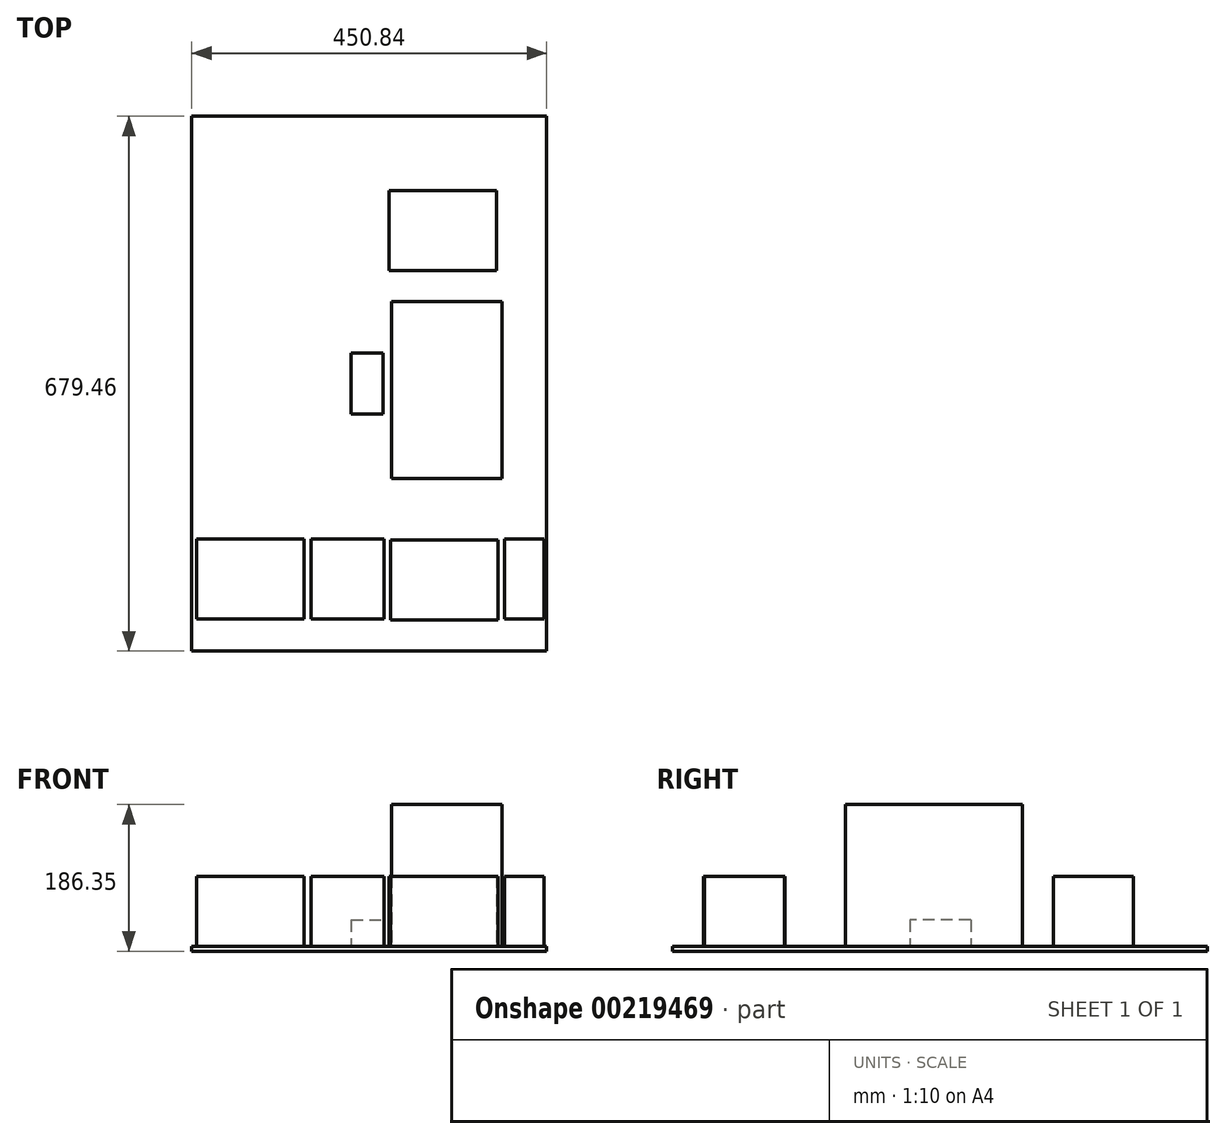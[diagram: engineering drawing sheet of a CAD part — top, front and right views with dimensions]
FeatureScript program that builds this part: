
annotation { "Feature Type Name" : "Feature", "Feature Type Description" : "" }
export const myFeature = defineFeature(function(context is Context, id is Id, definition is map)
    precondition{}
    {
        {
            var Q0;
            Q0=qCreatedBy(makeId("Top.planeOp"),FACE);
            var sketch = newSketch(context, id + "F0", { "sketchPlane" : qUnion([Q0])});
            skLineSegment(sketch, "E0.bottom", {"start": v(-225.42, -339.73) * mm, "end": v(225.43, -339.73) * mm});
            skLineSegment(sketch, "E0.top", {"start": v(-225.43, 339.72) * mm, "end": v(225.42, 339.72) * mm});
            skLineSegment(sketch, "E0.left", {"start": v(-225.42, -339.73) * mm, "end": v(-225.43, 339.73) * mm});
            skLineSegment(sketch, "E0.right", {"start": v(225.43, -339.73) * mm, "end": v(225.42, 339.72) * mm});
            skPoint(sketch, "E0.middle", {"position": v(0, 0) * mm});
            skSolve(sketch);
        }
        {
            var Q0;
            Q0=makeQuery(id+"F0.imprint","IMPRINT",FACE,{"disambiguationData":[TD([[makeQuery(id+"F0.imprint","IMPRINT",EDGE,{"derivedFrom":sQuery(id+"F0.wireOp",EDGE,"E0.bottom")}),1.0]])]});
            extrude(context, id + "F1", {"entities" : qUnion([Q0]), "oppositeDirection" : true, "depth" : 6.35 * mm});
        }
        {
            var Q0;
            Q0=makeQuery(id+"F1.opExtrude","CAP_FACE",FACE,{"disambiguationData":[OSD([sQuery(id+"F0.wireOp",EDGE,"E0.bottom"),sQuery(id+"F0.wireOp",EDGE,"E0.top"),sQuery(id+"F0.wireOp",EDGE,"E0.left"),sQuery(id+"F0.wireOp",EDGE,"E0.right")])],"isStart":true});
            var sketch = newSketch(context, id + "F2", { "sketchPlane" : qUnion([Q0])});
            skLineSegment(sketch, "E1.bottom", {"start": v(34.75, -122.57) * mm, "end": v(170.9, -122.57) * mm});
            skLineSegment(sketch, "E1.top", {"start": v(34.75, -224.17) * mm, "end": v(170.9, -224.17) * mm});
            skLineSegment(sketch, "E1.left", {"start": v(34.75, -122.57) * mm, "end": v(34.75, -224.17) * mm});
            skLineSegment(sketch, "E1.right", {"start": v(170.9, -122.57) * mm, "end": v(170.9, -224.17) * mm});
            skSolve(sketch);
        }
        {
            var Q0;
            Q0 = qSketchRegion(id + "F2", true);
            extrude(context, id + "F3", {"entities" : qUnion([Q0]), "depth" : 88.9 * mm, "offsetDistance" : 25.4 * mm});
        }
        {
            var Q0;
            Q0=makeQuery(id+"F1.opExtrude","CAP_FACE",FACE,{"disambiguationData":[OSD([sQuery(id+"F0.wireOp",EDGE,"E0.bottom"),sQuery(id+"F0.wireOp",EDGE,"E0.top"),sQuery(id+"F0.wireOp",EDGE,"E0.left"),sQuery(id+"F0.wireOp",EDGE,"E0.right")])],"isStart":true});
            var sketch = newSketch(context, id + "F4", { "sketchPlane" : qUnion([Q0])});
            skLineSegment(sketch, "E2.bottom", {"start": v(0, 209.73) * mm, "end": v(136.14, 209.73) * mm});
            skLineSegment(sketch, "E2.top", {"start": v(0, 108.13) * mm, "end": v(136.14, 108.13) * mm});
            skLineSegment(sketch, "E2.left", {"start": v(0, 209.73) * mm, "end": v(0, 108.13) * mm});
            skLineSegment(sketch, "E2.right", {"start": v(136.14, 209.73) * mm, "end": v(136.14, 108.13) * mm});
            skSolve(sketch);
        }
        {
            var Q0;
            Q0=makeQuery(id+"F4.imprint","IMPRINT",FACE,{"disambiguationData":[TD([[makeQuery(id+"F4.imprint","IMPRINT",EDGE,{"derivedFrom":sQuery(id+"F4.wireOp",EDGE,"E2.bottom")}),-1.0]])]});
            extrude(context, id + "F5", {"entities" : qUnion([Q0]), "depth" : 88.9 * mm, "offsetDistance" : 25.4 * mm});
        }
        {
            var Q0;
            Q0=makeQuery(id+"F1.opExtrude","CAP_FACE",FACE,{"disambiguationData":[OSD([sQuery(id+"F0.wireOp",EDGE,"E0.bottom"),sQuery(id+"F0.wireOp",EDGE,"E0.top"),sQuery(id+"F0.wireOp",EDGE,"E0.left"),sQuery(id+"F0.wireOp",EDGE,"E0.right")])],"isStart":true});
            var sketch = newSketch(context, id + "F6", { "sketchPlane" : qUnion([Q0])});
            skLineSegment(sketch, "E3.bottom", {"start": v(8.27, -126.38) * mm, "end": v(-41.51, -126.38) * mm});
            skLineSegment(sketch, "E3.top", {"start": v(8.27, -227.98) * mm, "end": v(-41.51, -227.98) * mm});
            skLineSegment(sketch, "E3.left", {"start": v(8.27, -126.38) * mm, "end": v(8.27, -227.98) * mm});
            skLineSegment(sketch, "E3.right", {"start": v(-41.51, -126.38) * mm, "end": v(-41.51, -227.98) * mm});
            skSolve(sketch);
        }
        {
            var Q0;
            Q0 = qSketchRegion(id + "F6", true);
            extrude(context, id + "F7", {"entities" : qUnion([Q0]), "depth" : 88.9 * mm, "offsetDistance" : 25.4 * mm});
        }
        {
            var Q0;
            Q0=makeQuery(id+"F1.opExtrude","CAP_FACE",FACE,{"disambiguationData":[OSD([sQuery(id+"F0.wireOp",EDGE,"E0.bottom"),sQuery(id+"F0.wireOp",EDGE,"E0.top"),sQuery(id+"F0.wireOp",EDGE,"E0.left"),sQuery(id+"F0.wireOp",EDGE,"E0.right")])],"isStart":true});
            var sketch = newSketch(context, id + "F8", { "sketchPlane" : qUnion([Q0])});
            skLineSegment(sketch, "E4.bottom", {"start": v(-221.8, -125.98) * mm, "end": v(-85.66, -125.98) * mm});
            skLineSegment(sketch, "E4.top", {"start": v(-221.8, -227.58) * mm, "end": v(-85.66, -227.58) * mm});
            skLineSegment(sketch, "E4.left", {"start": v(-221.8, -125.98) * mm, "end": v(-221.8, -227.58) * mm});
            skLineSegment(sketch, "E4.right", {"start": v(-85.66, -125.98) * mm, "end": v(-85.66, -227.58) * mm});
            skSolve(sketch);
        }
        {
            var Q0;
            Q0 = qSketchRegion(id + "F8", true);
            extrude(context, id + "F9", {"entities" : qUnion([Q0]), "depth" : 88.9 * mm, "offsetDistance" : 25.4 * mm});
        }
        {
            var Q0;
            Q0=makeQuery(id+"F3.opExtrude","SWEPT_BODY",BODY,{"disambiguationData":[OSD([sQuery(id+"F2.wireOp",EDGE,"E1.bottom"),sQuery(id+"F2.wireOp",EDGE,"E1.top"),sQuery(id+"F2.wireOp",EDGE,"E1.left"),sQuery(id+"F2.wireOp",EDGE,"E1.right")])]});
            transform(context, id + "F10", {"entities" : qUnion([Q0]), "transformType" : TransformType.TRANSLATION_3D, "dx" : -7.62 * mm, "dy" : -76.2 * mm, "dz" : 0 * mm, "makeCopy" : false});
        }
        {
            var Q0;
            Q0=makeQuery(id+"F7.opExtrude","SWEPT_BODY",BODY,{"disambiguationData":[OSD([sQuery(id+"F6.wireOp",EDGE,"E3.bottom"),sQuery(id+"F6.wireOp",EDGE,"E3.top"),sQuery(id+"F6.wireOp",EDGE,"E3.left"),sQuery(id+"F6.wireOp",EDGE,"E3.right")])]});
            transform(context, id + "F11", {"entities" : qUnion([Q0]), "transformType" : TransformType.TRANSLATION_3D, "dx" : 213.36 * mm, "dy" : -71.12 * mm, "dz" : 0 * mm, "makeCopy" : false});
        }
        {
            var Q0;
            Q0=makeQuery(id+"F9.opExtrude","SWEPT_BODY",BODY,{"disambiguationData":[OSD([sQuery(id+"F8.wireOp",EDGE,"E4.bottom"),sQuery(id+"F8.wireOp",EDGE,"E4.top"),sQuery(id+"F8.wireOp",EDGE,"E4.left"),sQuery(id+"F8.wireOp",EDGE,"E4.right")])]});
            transform(context, id + "F12", {"entities" : qUnion([Q0]), "transformType" : TransformType.TRANSLATION_3D, "dx" : 2.54 * mm, "dy" : -71.12 * mm, "dz" : 0 * mm, "makeCopy" : false});
        }
        {
            var Q0;
            Q0=makeQuery(id+"F1.opExtrude","CAP_FACE",FACE,{"disambiguationData":[OSD([sQuery(id+"F0.wireOp",EDGE,"E0.bottom"),sQuery(id+"F0.wireOp",EDGE,"E0.top"),sQuery(id+"F0.wireOp",EDGE,"E0.left"),sQuery(id+"F0.wireOp",EDGE,"E0.right")])],"isStart":true});
            var sketch = newSketch(context, id + "F13", { "sketchPlane" : qUnion([Q0])});
            skLineSegment(sketch, "E5.bottom", {"start": v(-109.58, -197.58) * mm, "end": v(-16.62, -197.58) * mm});
            skLineSegment(sketch, "E5.top", {"start": v(-109.58, -299.18) * mm, "end": v(-16.62, -299.18) * mm});
            skLineSegment(sketch, "E5.left", {"start": v(-109.58, -197.58) * mm, "end": v(-109.58, -299.18) * mm});
            skLineSegment(sketch, "E5.right", {"start": v(-16.62, -197.58) * mm, "end": v(-16.62, -299.18) * mm});
            skSolve(sketch);
        }
        {
            var Q0;
            Q0=makeQuery(id+"F13.imprint","IMPRINT",FACE,{"disambiguationData":[TD([[makeQuery(id+"F13.imprint","IMPRINT",EDGE,{"derivedFrom":sQuery(id+"F13.wireOp",EDGE,"E5.bottom")}),-1.0]])]});
            extrude(context, id + "F14", {"entities" : qUnion([Q0]), "depth" : 88.9 * mm, "offsetDistance" : 25.4 * mm});
        }
        {
            var Q0;
            Q0=makeQuery(id+"F14.opExtrude","SWEPT_BODY",BODY,{"disambiguationData":[OSD([sQuery(id+"F13.wireOp",EDGE,"E5.bottom"),sQuery(id+"F13.wireOp",EDGE,"E5.top"),sQuery(id+"F13.wireOp",EDGE,"E5.left"),sQuery(id+"F13.wireOp",EDGE,"E5.right")])]});
            transform(context, id + "F15", {"entities" : qUnion([Q0]), "transformType" : TransformType.TRANSLATION_3D, "dx" : 35.56 * mm, "dy" : 0 * mm, "dz" : 0 * mm, "makeCopy" : false});
        }
        {
            var Q0;
            Q0=makeQuery(id+"F1.opExtrude","CAP_FACE",FACE,{"disambiguationData":[OSD([sQuery(id+"F0.wireOp",EDGE,"E0.bottom"),sQuery(id+"F0.wireOp",EDGE,"E0.top"),sQuery(id+"F0.wireOp",EDGE,"E0.left"),sQuery(id+"F0.wireOp",EDGE,"E0.right")])],"isStart":true});
            var sketch = newSketch(context, id + "F16", { "sketchPlane" : qUnion([Q0])});
            skLineSegment(sketch, "E6.bottom", {"start": v(30.9, 61.35) * mm, "end": v(170.9, 61.35) * mm});
            skLineSegment(sketch, "E6.top", {"start": v(30.9, -163.65) * mm, "end": v(170.9, -163.65) * mm});
            skLineSegment(sketch, "E6.left", {"start": v(30.9, 61.35) * mm, "end": v(30.9, -163.65) * mm});
            skLineSegment(sketch, "E6.right", {"start": v(170.9, 61.35) * mm, "end": v(170.9, -163.65) * mm});
            skSolve(sketch);
        }
        {
            var Q0;
            Q0 = qSketchRegion(id + "F16", true);
            extrude(context, id + "F17", {"entities" : qUnion([Q0]), "depth" : 180 * mm, "offsetDistance" : 25.4 * mm});
        }
        {
            var Q0;
            Q0=makeQuery(id+"F1.opExtrude","CAP_FACE",FACE,{"disambiguationData":[OSD([sQuery(id+"F0.wireOp",EDGE,"E0.bottom"),sQuery(id+"F0.wireOp",EDGE,"E0.top"),sQuery(id+"F0.wireOp",EDGE,"E0.left"),sQuery(id+"F0.wireOp",EDGE,"E0.right")])],"isStart":true});
            var sketch = newSketch(context, id + "F18", { "sketchPlane" : qUnion([Q0])});
            skLineSegment(sketch, "E7.bottom", {"start": v(-40.64, -93.26) * mm, "end": v(0, -93.26) * mm});
            skLineSegment(sketch, "E7.top", {"start": v(-40.64, -170.47) * mm, "end": v(0, -170.47) * mm});
            skLineSegment(sketch, "E7.left", {"start": v(-40.64, -93.26) * mm, "end": v(-40.64, -170.47) * mm});
            skLineSegment(sketch, "E7.right", {"start": v(0, -93.26) * mm, "end": v(0, -170.47) * mm});
            skSolve(sketch);
        }
        {
            var Q0;
            Q0=makeQuery(id+"F18.imprint","IMPRINT",FACE,{"disambiguationData":[TD([[makeQuery(id+"F18.imprint","IMPRINT",EDGE,{"derivedFrom":sQuery(id+"F18.wireOp",EDGE,"E7.bottom")}),-1.0]])]});
            extrude(context, id + "F19", {"entities" : qUnion([Q0]), "depth" : 33.27 * mm, "offsetDistance" : 25.4 * mm});
        }
        {
            var Q0;
            Q0=makeQuery(id+"F17.opExtrude","SWEPT_BODY",BODY,{"disambiguationData":[OSD([sQuery(id+"F16.wireOp",EDGE,"E6.bottom"),sQuery(id+"F16.wireOp",EDGE,"E6.top"),sQuery(id+"F16.wireOp",EDGE,"E6.left"),sQuery(id+"F16.wireOp",EDGE,"E6.right")])]});
            transform(context, id + "F20", {"entities" : qUnion([Q0]), "transformType" : TransformType.TRANSLATION_3D, "dx" : -2.54 * mm, "dy" : 43.18 * mm, "dz" : 0 * mm, "makeCopy" : false});
        }
        {
            var Q0;
            Q0=makeQuery(id+"F5.opExtrude","SWEPT_BODY",BODY,{"disambiguationData":[OSD([sQuery(id+"F4.wireOp",EDGE,"E2.bottom"),sQuery(id+"F4.wireOp",EDGE,"E2.top"),sQuery(id+"F4.wireOp",EDGE,"E2.left"),sQuery(id+"F4.wireOp",EDGE,"E2.right")])]});
            transform(context, id + "F21", {"entities" : qUnion([Q0]), "transformType" : TransformType.TRANSLATION_3D, "dx" : 25.4 * mm, "dy" : 35.56 * mm, "dz" : 0 * mm, "makeCopy" : false});
        }
        {
            var Q0;
            Q0=makeQuery(id+"F19.opExtrude","SWEPT_BODY",BODY,{"disambiguationData":[OSD([sQuery(id+"F18.wireOp",EDGE,"E7.bottom"),sQuery(id+"F18.wireOp",EDGE,"E7.top"),sQuery(id+"F18.wireOp",EDGE,"E7.left"),sQuery(id+"F18.wireOp",EDGE,"E7.right")])]});
            transform(context, id + "F22", {"entities" : qUnion([Q0]), "transformType" : TransformType.TRANSLATION_3D, "dx" : 17.78 * mm, "dy" : 132.08 * mm, "dz" : 0 * mm, "makeCopy" : false});
        }
    });
